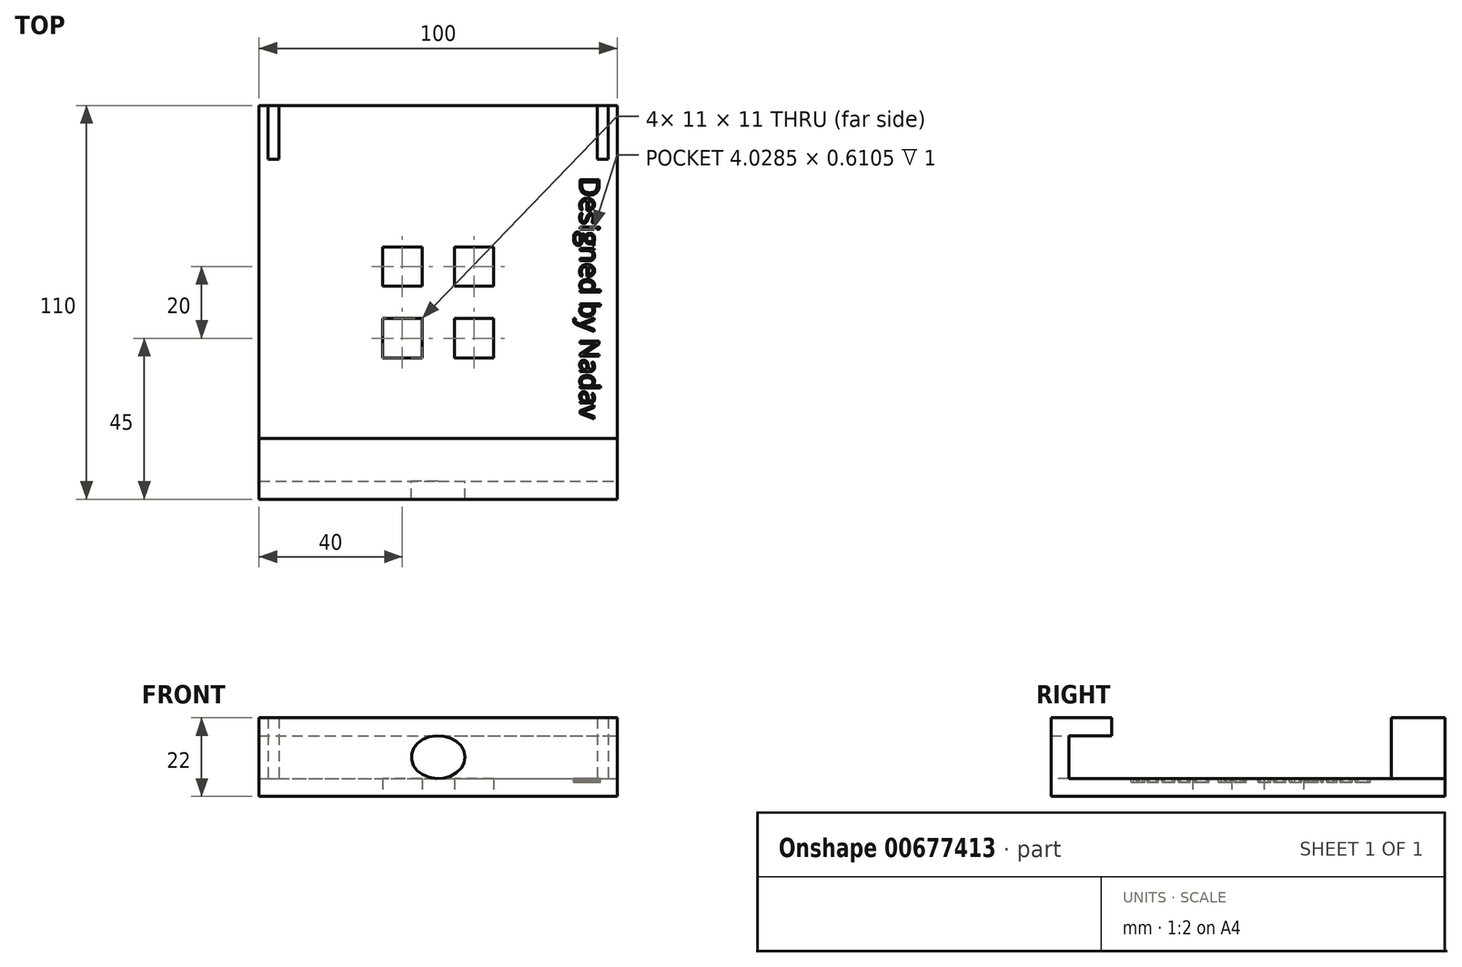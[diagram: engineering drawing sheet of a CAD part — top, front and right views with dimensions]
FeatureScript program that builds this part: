
annotation { "Feature Type Name" : "Feature", "Feature Type Description" : "" }
export const myFeature = defineFeature(function(context is Context, id is Id, definition is map)
    precondition{}
    {
        {
            var Q0;
            Q0=qCreatedBy(makeId("Top.planeOp"),FACE);
            var sketch = newSketch(context, id + "F0", { "sketchPlane" : qUnion([Q0])});
            skLineSegment(sketch, "E0.bottom", {"start": v(-50, 55) * mm, "end": v(50, 55) * mm});
            skLineSegment(sketch, "E0.top", {"start": v(-50, -55) * mm, "end": v(50, -55) * mm});
            skLineSegment(sketch, "E0.left", {"start": v(-50, 55) * mm, "end": v(-50, -55) * mm});
            skLineSegment(sketch, "E0.right", {"start": v(50, 55) * mm, "end": v(50, -55) * mm});
            skPoint(sketch, "E1", {"position": v(0, -55) * mm});
            skLineSegment(sketch, "E2", {"start": v(0, 0) * mm, "end": v(0, -55) * mm, "construction": true});
            skLineSegment(sketch, "E3.bottom", {"start": v(10, 10) * mm, "end": v(-10, 10) * mm, "construction": true});
            skLineSegment(sketch, "E3.top", {"start": v(10, -10) * mm, "end": v(-10, -10) * mm, "construction": true});
            skLineSegment(sketch, "E3.left", {"start": v(10, 10) * mm, "end": v(10, -10) * mm, "construction": true});
            skLineSegment(sketch, "E3.right", {"start": v(-10, 10) * mm, "end": v(-10, -10) * mm, "construction": true});
            skPoint(sketch, "E3.middle", {"position": v(0, 0) * mm});
            skLineSegment(sketch, "E4.bottom", {"start": v(-4.5, 15.5) * mm, "end": v(-15.5, 15.5) * mm});
            skLineSegment(sketch, "E4.top", {"start": v(-4.5, 4.5) * mm, "end": v(-15.5, 4.5) * mm});
            skLineSegment(sketch, "E4.left", {"start": v(-4.5, 15.5) * mm, "end": v(-4.5, 4.5) * mm});
            skLineSegment(sketch, "E4.right", {"start": v(-15.5, 15.5) * mm, "end": v(-15.5, 4.5) * mm});
            skPoint(sketch, "E4.middle", {"position": v(-10, 10) * mm});
            skLineSegment(sketch, "E5.bottom", {"start": v(15.5, 15.5) * mm, "end": v(4.5, 15.5) * mm});
            skLineSegment(sketch, "E5.top", {"start": v(15.5, 4.5) * mm, "end": v(4.5, 4.5) * mm});
            skLineSegment(sketch, "E5.left", {"start": v(15.5, 15.5) * mm, "end": v(15.5, 4.5) * mm});
            skLineSegment(sketch, "E5.right", {"start": v(4.5, 15.5) * mm, "end": v(4.5, 4.5) * mm});
            skPoint(sketch, "E5.middle", {"position": v(10, 10) * mm});
            skLineSegment(sketch, "E6.bottom", {"start": v(15.5, -4.5) * mm, "end": v(4.5, -4.5) * mm});
            skLineSegment(sketch, "E6.top", {"start": v(15.5, -15.5) * mm, "end": v(4.5, -15.5) * mm});
            skLineSegment(sketch, "E6.left", {"start": v(15.5, -4.5) * mm, "end": v(15.5, -15.5) * mm});
            skLineSegment(sketch, "E6.right", {"start": v(4.5, -4.5) * mm, "end": v(4.5, -15.5) * mm});
            skPoint(sketch, "E6.middle", {"position": v(10, -10) * mm});
            skLineSegment(sketch, "E7.bottom", {"start": v(-4.5, -4.5) * mm, "end": v(-15.5, -4.5) * mm});
            skLineSegment(sketch, "E7.top", {"start": v(-4.5, -15.5) * mm, "end": v(-15.5, -15.5) * mm});
            skLineSegment(sketch, "E7.left", {"start": v(-4.5, -4.5) * mm, "end": v(-4.5, -15.5) * mm});
            skLineSegment(sketch, "E7.right", {"start": v(-15.5, -4.5) * mm, "end": v(-15.5, -15.5) * mm});
            skPoint(sketch, "E7.middle", {"position": v(-10, -10) * mm});
            skSolve(sketch);
        }
        {
            var Q0;
            Q0=makeQuery(id+"F0.imprint","IMPRINT",FACE,{"disambiguationData":[TD([[makeQuery(id+"F0.imprint","IMPRINT",EDGE,{"derivedFrom":sQuery(id+"F0.wireOp",EDGE,"E0.top")}),1.0]])]});
            var Q1;
            {var subQ5=makeQuery(id+"F8eZvwuiHdmqwXy_1.opExtrude","CAP_EDGE",EDGE,{"disambiguationData":[OSD([sQuery(id+"FpGw7YJ82lAfyMx_1.wireOp",EDGE,"hrqeKWLc-j1Me-NRp5-MnrF-pfZAyydPzFUx.top")])],"isStart":false});Q1=makeQuery(id+"F0.imprint","IMPRINT",FACE,{"disambiguationData":[TD([[makeQuery(id+"F0.imprint","IMPRINT",EDGE,{"derivedFrom":subQ5}),-1.0]])]});}
            extrude(context, id + "F1", {"entities" : qUnion([Q0, Q1]), "depth" : 5 * mm, "offsetDistance" : 25 * mm});
        }
        {
            var Q0;
            Q0=makeQuery(id+"F1.opExtrude","CAP_FACE",FACE,{"disambiguationData":[OSD([sQuery(id+"F0.wireOp",EDGE,"E0.bottom"),sQuery(id+"F0.wireOp",EDGE,"E0.top"),sQuery(id+"F0.wireOp",EDGE,"E0.left"),sQuery(id+"F0.wireOp",EDGE,"E0.right")])],"isStart":false});
            var sketch = newSketch(context, id + "F2", { "sketchPlane" : qUnion([Q0])});
            skLineSegment(sketch, "E8.bottom", {"start": v(-50, -50) * mm, "end": v(50, -50) * mm});
            skLineSegment(sketch, "E8.top", {"start": v(-50, -55) * mm, "end": v(50, -55) * mm});
            skLineSegment(sketch, "E8.left", {"start": v(-50, -50) * mm, "end": v(-50, -55) * mm});
            skLineSegment(sketch, "E8.right", {"start": v(50, -50) * mm, "end": v(50, -55) * mm});
            skLineSegment(sketch, "E9.bottom", {"start": v(-47.5, 55) * mm, "end": v(-44.5, 55) * mm});
            skLineSegment(sketch, "E9.top", {"start": v(-47.5, 40) * mm, "end": v(-44.5, 40) * mm});
            skLineSegment(sketch, "E9.left", {"start": v(-44.5, 55) * mm, "end": v(-44.5, 40) * mm});
            skLineSegment(sketch, "E9.right", {"start": v(-47.5, 55) * mm, "end": v(-47.5, 40) * mm});
            skLineSegment(sketch, "E10.bottom", {"start": v(44.5, 55) * mm, "end": v(47.5, 55) * mm});
            skLineSegment(sketch, "E10.top", {"start": v(44.5, 40) * mm, "end": v(47.5, 40) * mm});
            skLineSegment(sketch, "E10.left", {"start": v(47.5, 55) * mm, "end": v(47.5, 40) * mm});
            skLineSegment(sketch, "E10.right", {"start": v(44.5, 55) * mm, "end": v(44.5, 40) * mm});
            skLineSegment(sketch, "E11", {"start": v(-29.54, 40) * mm, "end": v(-29.54, -50) * mm, "construction": true});
            skLineSegment(sketch, "E12", {"start": v(-47.5, 40) * mm, "end": v(47.5, 40) * mm, "construction": true});
            skSolve(sketch);
        }
        {
            var Q0;
            Q0=makeQuery(id+"F2.imprint","IMPRINT",FACE,{"disambiguationData":[TD([[makeQuery(id+"F2.imprint","IMPRINT",EDGE,{"derivedFrom":sQuery(id+"F2.wireOp",EDGE,"E9.bottom")}),-1.0]])]});
            var Q1;
            Q1=makeQuery(id+"F2.imprint","IMPRINT",FACE,{"disambiguationData":[TD([[makeQuery(id+"F2.imprint","IMPRINT",EDGE,{"derivedFrom":sQuery(id+"F2.wireOp",EDGE,"E10.bottom")}),-1.0]])]});
            var Q2;
            Q2=makeQuery(id+"F2.imprint","IMPRINT",FACE,{"disambiguationData":[TD([[makeQuery(id+"F2.imprint","IMPRINT",EDGE,{"derivedFrom":sQuery(id+"F2.wireOp",EDGE,"E8.bottom")}),-1.0]])]});
            extrude(context, id + "F3", {"entities" : qUnion([Q0, Q1, Q2]), "operationType" : NewBodyOperationType.ADD, "depth" : 17 * mm, "offsetDistance" : 25 * mm});
        }
        {
            var Q0;
            Q0=makeQuery(id+"F3.opExtrude","SWEPT_FACE",FACE,{"disambiguationData":[OSD([sQuery(id+"F2.wireOp",EDGE,"E8.bottom")])]});
            var sketch = newSketch(context, id + "F4", { "sketchPlane" : qUnion([Q0])});
            skLineSegment(sketch, "E13.bottom", {"start": v(50, 17) * mm, "end": v(-50, 17) * mm});
            skLineSegment(sketch, "E13.top", {"start": v(50, 22) * mm, "end": v(-50, 22) * mm});
            skLineSegment(sketch, "E13.left", {"start": v(50, 17) * mm, "end": v(50, 22) * mm});
            skLineSegment(sketch, "E13.right", {"start": v(-50, 17) * mm, "end": v(-50, 22) * mm});
            skLineSegment(sketch, "E14", {"start": v(0, 5) * mm, "end": v(0, 17) * mm, "construction": true});
            skPoint(sketch, "E15", {"position": v(0, 11) * mm});
            skEllipse(sketch, "E16", {"center": v(0, 11) * mm, "majorRadius": 7.5 * mm, "minorRadius": 6 * mm, "majorAxis": v(-1, 0)});
            skLineSegment(sketch, "E17", {"start": v(-7.5, 5) * mm, "end": v(-7.5, 17) * mm, "construction": true});
            skLineSegment(sketch, "E18", {"start": v(7.5, 5) * mm, "end": v(7.5, 17) * mm, "construction": true});
            skPoint(sketch, "E18.endSnap0", {"position": v(7.5, 11) * mm});
            skSolve(sketch);
        }
        {
            var Q0;
            Q0=makeQuery(id+"F4.imprint","IMPRINT",FACE,{"disambiguationData":[TD([[makeQuery(id+"F4.imprint","IMPRINT",EDGE,{"derivedFrom":sQuery(id+"F4.wireOp",EDGE,"E13.bottom")}),-1.0]])]});
            extrude(context, id + "F5", {"entities" : qUnion([Q0]), "operationType" : NewBodyOperationType.ADD, "depth" : 12 * mm, "offsetDistance" : 25 * mm});
        }
        {
            var Q0;
            {var subQ0=sQuery(id+"F4.wireOp",EDGE,"E16");var subQ1=makeQuery(id+"F4.imprint","INTERSECT",VERTEX,{"derivedFrom":[sQuery(id+"F4.wireOp",EDGE,"E13.bottom"),subQ0]});Q0=makeQuery(id+"F4.imprint","IMPRINT",FACE,{"disambiguationData":[TD([[makeQuery(id+"F4.imprint","IMPRINT",EDGE,{"disambiguationData":[TD([[subQ1,1.0]])],"derivedFrom":subQ0}),1.0]])]});}
            extrude(context, id + "F6", {"entities" : qUnion([Q0]), "operationType" : NewBodyOperationType.REMOVE, "oppositeDirection" : true, "depth" : 25 * mm, "offsetDistance" : 25 * mm});
        }
        {
            var Q0;
            Q0=makeQuery(id+"F1.opExtrude","CAP_FACE",FACE,{"disambiguationData":[OSD([sQuery(id+"F0.wireOp",EDGE,"E0.bottom"),sQuery(id+"F0.wireOp",EDGE,"E0.top"),sQuery(id+"F0.wireOp",EDGE,"E0.left"),sQuery(id+"F0.wireOp",EDGE,"E0.right")])],"isStart":false});
            var sketch = newSketch(context, id + "F7", { "sketchPlane" : qUnion([Q0])});
            skText(sketch, "E19", { "text": "Designed by Nadav", "fontName": "OpenSans-Regular.ttf"});
            const initialGuessF7  = {"E19": [0.03958, 0.035, 0, -1, 0.00542]};
            skSetInitialGuess(sketch, initialGuessF7);
            skSolve(sketch);
        }
        {
            var Q0;
            Q0=qSketchRegion(id+"F7",true);
            extrude(context, id + "F8", {"entities" : qUnion([Q0]), "operationType" : NewBodyOperationType.REMOVE, "oppositeDirection" : true, "depth" : 1 * mm, "offsetDistance" : 25 * mm});
        }
    });
